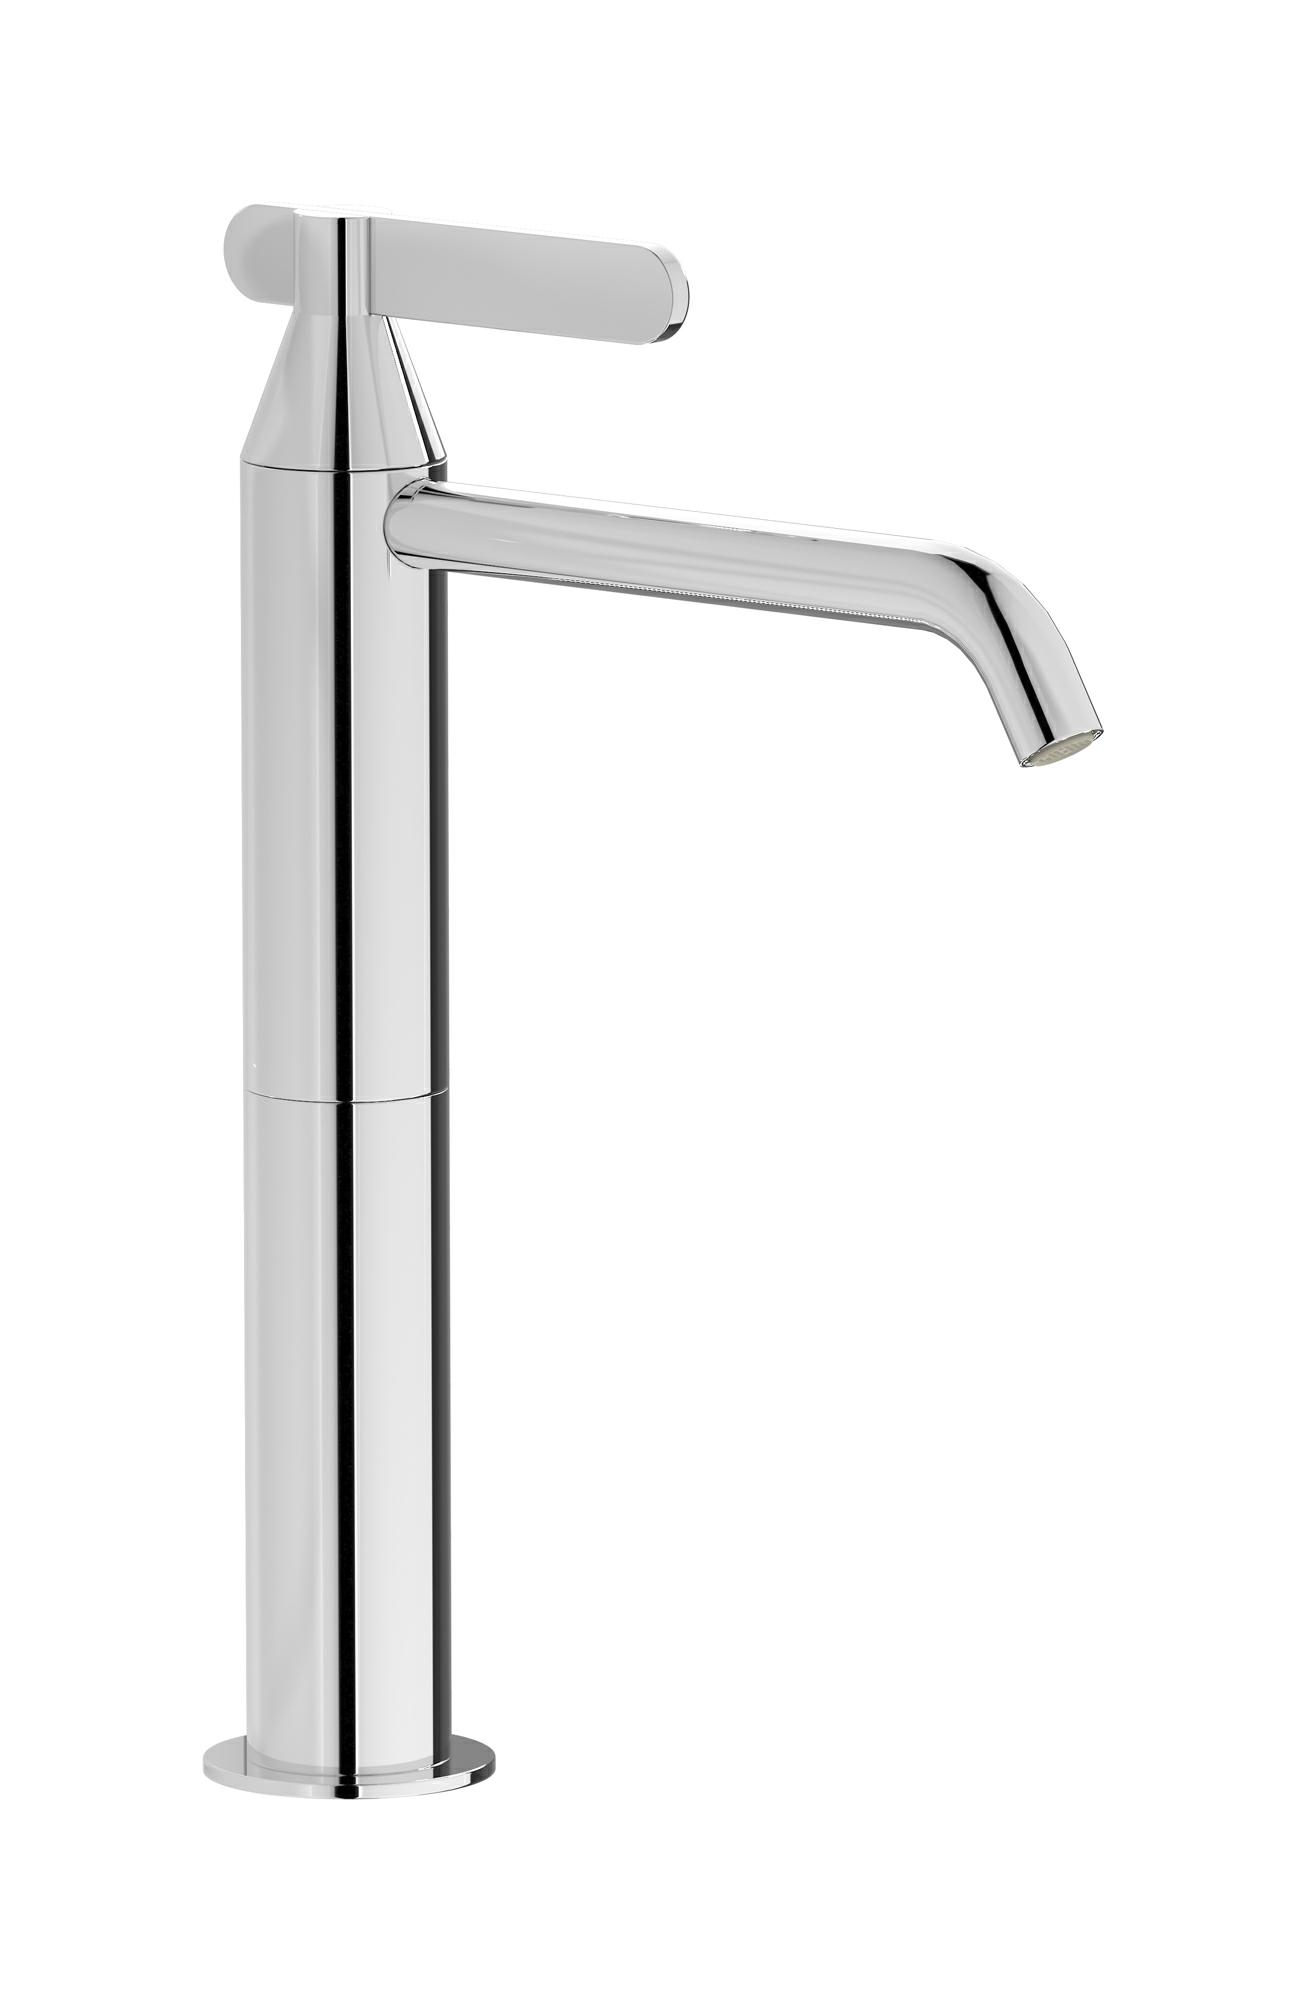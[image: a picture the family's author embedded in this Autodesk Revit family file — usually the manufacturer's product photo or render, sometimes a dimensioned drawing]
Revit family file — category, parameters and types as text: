
# Revit family: OH370
name_source: partatom
category: Apparecchi idraulici
units: mm (PartAtom-declared; Revit-internal decimal feet)

## family parameters
Basato su piano di lavoro = No
Condiviso = No
Mantieni orientamento annotazione = No
Numero OmniClass = 23.45.55.17
Punto di calcolo locali = No
Quota connettore circolare = Usa diametro
Sempre verticale = Sì
Taglio con vuoti quando caricato = No
Tipo di parte = Normale
Titolo OmniClass = Mixing Faucets

## types (6) — shared parameters
Cold water inlet = 10 mm  [stored 0.0328084 ft]
Commenti sul tipo = Single lever kitchen mixer
Connessione CW = No
Connessione HW = No
Connessione di scarico = No
Connessione di ventilazione = No
Descrizione = Single lever kitchen mixer
Hot water inlet = 10 mm  [stored 0.0328084 ft]
Produttore = IB Rubinetterie S.p.A.
URL = https://www.weareib.it
zero-valued in all types: Prospetto di default

## per-type parameters (varying)
| type | Finishes surface | Immagine tipo | Modello |
| Chrome | IB_Chrome | OH370CC.jpg | OH370CC |
| Brushed Black Chrome | IB_Brushed black chrome | OH370CS.jpg | OH370CS |
| Brushed Pale Gold | IB_brushed pale gold | OH370IS.jpg | OH370IS |
| Natural Brass | IB_Brass | OH370ON.jpg | OH370ON |
| Brushed Rose Gold | IB_Brushed rose gold | OH370SR.jpg | OH370SR |
| Brushed Nickel | IB_Brushed nickel | OH370SS.jpg | OH370SS |

note: [stored X ft] marks values corroborated as IEEE doubles in the binary element streams (Revit-internal decimal feet)
